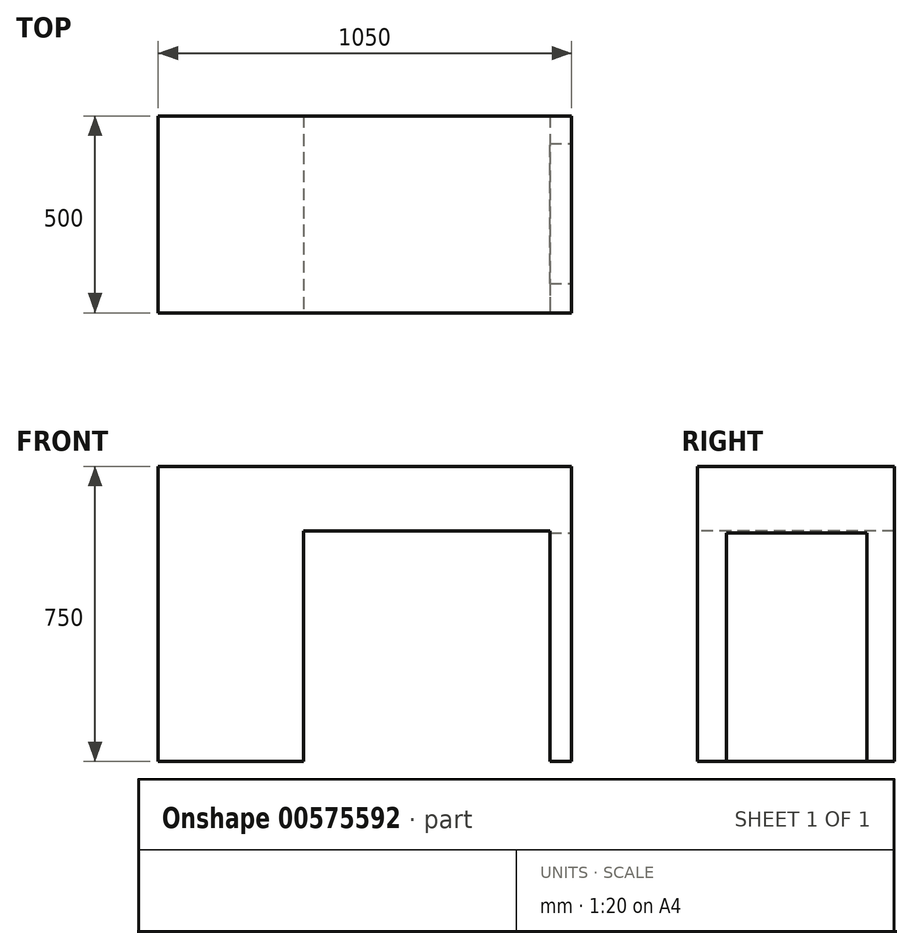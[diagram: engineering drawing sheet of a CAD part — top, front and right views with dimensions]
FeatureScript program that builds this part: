
annotation { "Feature Type Name" : "Feature", "Feature Type Description" : "" }
export const myFeature = defineFeature(function(context is Context, id is Id, definition is map)
    precondition{}
    {
        {
            var Q0;
            Q0=qCreatedBy(makeId("Top.planeOp"),FACE);
            var sketch = newSketch(context, id + "F0", { "sketchPlane" : qUnion([Q0])});
            skLineSegment(sketch, "E0.bottom", {"start": v(0, 0) * mm, "end": v(-1050, 0) * mm});
            skLineSegment(sketch, "E0.top", {"start": v(0, 500) * mm, "end": v(-1050, 500) * mm});
            skLineSegment(sketch, "E0.left", {"start": v(0, 0) * mm, "end": v(0, 500) * mm});
            skLineSegment(sketch, "E0.right", {"start": v(-1050, 0) * mm, "end": v(-1050, 500) * mm});
            skSolve(sketch);
        }
        {
            var Q0;
            Q0 = qSketchRegion(id + "F0", true);
            extrude(context, id + "F1", {"entities" : qUnion([Q0]), "depth" : 750 * mm, "offsetDistance" : 25 * mm});
        }
        {
            var Q0;
            Q0=makeQuery(id+"F1.opExtrude","SWEPT_FACE",FACE,{"disambiguationData":[OSD([sQuery(id+"F0.wireOp",EDGE,"E0.bottom")])]});
            var sketch = newSketch(context, id + "F2", { "sketchPlane" : qUnion([Q0])});
            skLineSegment(sketch, "E1.bottom", {"start": v(-54.96, 0) * mm, "end": v(-680.6, 0) * mm});
            skLineSegment(sketch, "E1.top", {"start": v(-54.96, 585.84) * mm, "end": v(-680.6, 585.84) * mm});
            skLineSegment(sketch, "E1.left", {"start": v(-54.96, 0) * mm, "end": v(-54.96, 585.84) * mm});
            skLineSegment(sketch, "E1.right", {"start": v(-680.6, 0) * mm, "end": v(-680.6, 585.84) * mm});
            skSolve(sketch);
        }
        {
            var Q0;
            Q0 = qSketchRegion(id + "F2", true);
            extrude(context, id + "F3", {"entities" : qUnion([Q0]), "operationType" : NewBodyOperationType.REMOVE, "endBound" : BoundingType.UP_TO_NEXT, "oppositeDirection" : true, "depth" : 25 * mm, "offsetDistance" : 25 * mm});
        }
        {
            var Q0;
            Q0=makeQuery(id+"F1.opExtrude","SWEPT_FACE",FACE,{"disambiguationData":[OSD([sQuery(id+"F0.wireOp",EDGE,"E0.left")])]});
            var sketch = newSketch(context, id + "F4", { "sketchPlane" : qUnion([Q0])});
            skLineSegment(sketch, "E2.bottom", {"start": v(430.37, 0) * mm, "end": v(74.21, 0) * mm});
            skLineSegment(sketch, "E2.top", {"start": v(430.37, 580.15) * mm, "end": v(74.21, 580.15) * mm});
            skLineSegment(sketch, "E2.left", {"start": v(430.37, 0) * mm, "end": v(430.37, 580.15) * mm});
            skLineSegment(sketch, "E2.right", {"start": v(74.21, 0) * mm, "end": v(74.21, 580.15) * mm});
            skSolve(sketch);
        }
        {
            var Q0;
            Q0 = qSketchRegion(id + "F4", true);
            extrude(context, id + "F5", {"entities" : qUnion([Q0]), "operationType" : NewBodyOperationType.REMOVE, "endBound" : BoundingType.UP_TO_NEXT, "oppositeDirection" : true, "depth" : 25 * mm, "offsetDistance" : 25 * mm});
        }
    });
